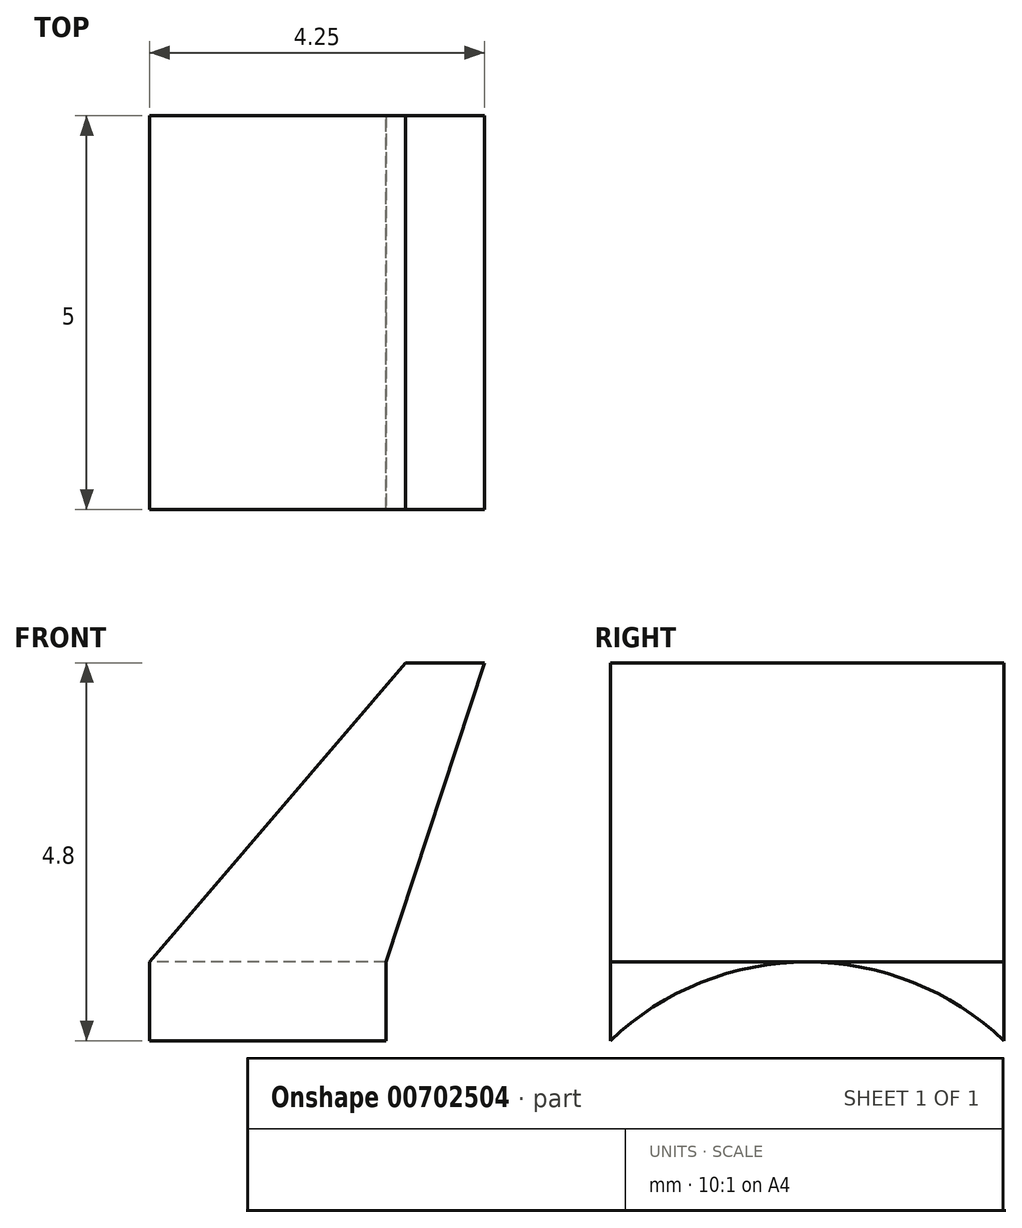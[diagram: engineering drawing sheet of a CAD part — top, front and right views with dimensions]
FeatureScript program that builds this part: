
annotation { "Feature Type Name" : "Feature", "Feature Type Description" : "" }
export const myFeature = defineFeature(function(context is Context, id is Id, definition is map)
    precondition{}
    {
        {
            var Q0;
            Q0=qCreatedBy(makeId("Front.planeOp"),FACE);
            var sketch = newSketch(context, id + "F0", { "sketchPlane" : qUnion([Q0])});
            skLineSegment(sketch, "E0", {"start": v(0, 0) * mm, "end": v(3, 0) * mm});
            skLineSegment(sketch, "E1", {"start": v(3, 0) * mm, "end": v(4.25, 3.8) * mm});
            skLineSegment(sketch, "E2", {"start": v(4.25, 3.8) * mm, "end": v(3.25, 3.8) * mm});
            skLineSegment(sketch, "E3", {"start": v(3.25, 3.8) * mm, "end": v(0, 0) * mm});
            skSolve(sketch);
        }
        {
            var Q0;
            Q0=makeQuery(id+"F0.imprint","IMPRINT",FACE,{"disambiguationData":[TD([[makeQuery(id+"F0.imprint","IMPRINT",EDGE,{"derivedFrom":sQuery(id+"F0.wireOp",EDGE,"E0")}),1.0]])]});
            extrude(context, id + "F1", {"entities" : qUnion([Q0]), "depth" : 5 * mm, "offsetDistance" : 25 * mm});
        }
        {
            var Q0;
            Q0=makeQuery(id+"F1.opExtrude","SWEPT_FACE",FACE,{"disambiguationData":[OSD([sQuery(id+"F0.wireOp",EDGE,"E0")])]});
            extrude(context, id + "F2", {"entities" : qUnion([Q0]), "operationType" : NewBodyOperationType.ADD, "depth" : 1 * mm, "offsetDistance" : 25 * mm});
        }
        {
            var Q0;
            Q0=makeQuery(id+"F2.opExtrude","SWEPT_FACE",FACE,{"disambiguationData":[OSD([sQuery(id+"F0.wireOp",EDGE,"E0"),sQuery(id+"F0.wireOp",EDGE,"E3")])]});
            var sketch = newSketch(context, id + "F3", { "sketchPlane" : qUnion([Q0])});
            skArc(sketch, "E4", {"start": v(5, -1) * mm, "mid": v(2.5, 0) * mm, "end": v(0, -1) * mm});
            skSolve(sketch);
        }
        {
            var Q0;
            {var subQ1=sQuery(id+"F0.wireOp",EDGE,"E3");var subQ2=sQuery(id+"F0.wireOp",EDGE,"E0");var subQ3=makeQuery(id+"F2.opExtrude","CAP_EDGE",EDGE,{"disambiguationData":[OSD([subQ2,subQ1])],"isStart":false});Q0=makeQuery(id+"F3.imprint","IMPRINT",FACE,{"disambiguationData":[TD([[makeQuery(id+"F3.imprint","IMPRINT",EDGE,{"derivedFrom":subQ3}),-1.0]])]});}
            extrude(context, id + "F4", {"entities" : qUnion([Q0]), "operationType" : NewBodyOperationType.REMOVE, "oppositeDirection" : true, "depth" : 25 * mm, "offsetDistance" : 25 * mm});
        }
    });
